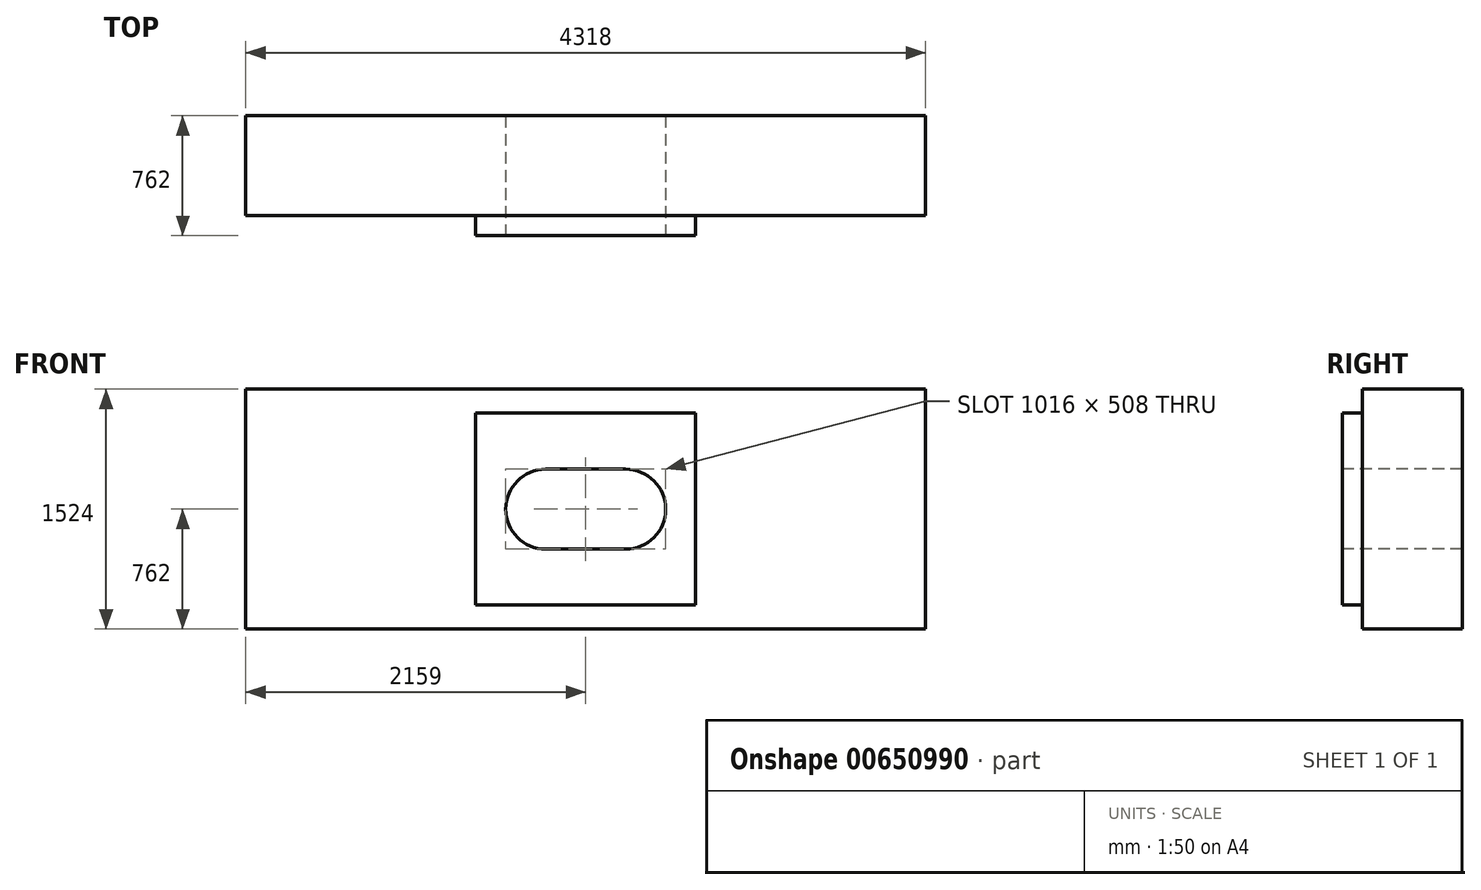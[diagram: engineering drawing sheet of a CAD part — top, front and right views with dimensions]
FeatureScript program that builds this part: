
annotation { "Feature Type Name" : "Feature", "Feature Type Description" : "" }
export const myFeature = defineFeature(function(context is Context, id is Id, definition is map)
    precondition{}
    {
        {
            var Q0;
            Q0=qCreatedBy(makeId("Front.planeOp"),FACE);
            var sketch = newSketch(context, id + "F0", { "sketchPlane" : qUnion([Q0])});
            skLineSegment(sketch, "E0.bottom", {"start": v(2159, -762) * mm, "end": v(-2159, -762) * mm});
            skLineSegment(sketch, "E0.top", {"start": v(2159, 762) * mm, "end": v(-2159, 762) * mm});
            skLineSegment(sketch, "E0.left", {"start": v(2159, -762) * mm, "end": v(2159, 762) * mm});
            skLineSegment(sketch, "E0.right", {"start": v(-2159, -762) * mm, "end": v(-2159, 762) * mm});
            skPoint(sketch, "E0.middle", {"position": v(0, 0) * mm});
            skSolve(sketch);
        }
        {
            var Q0;
            Q0=makeQuery(id+"F0.imprint","IMPRINT",FACE,{"disambiguationData":[TD([[makeQuery(id+"F0.imprint","IMPRINT",EDGE,{"derivedFrom":sQuery(id+"F0.wireOp",EDGE,"E0.bottom")}),-1.0]])]});
            extrude(context, id + "F1", {"entities" : qUnion([Q0]), "depth" : 635 * mm, "offsetDistance" : 25.4 * mm});
        }
        {
            var Q0;
            Q0=makeQuery(id+"F1.opExtrude","CAP_FACE",FACE,{"disambiguationData":[OSD([sQuery(id+"F0.wireOp",EDGE,"E0.bottom"),sQuery(id+"F0.wireOp",EDGE,"E0.top"),sQuery(id+"F0.wireOp",EDGE,"E0.left"),sQuery(id+"F0.wireOp",EDGE,"E0.right")])],"isStart":false});
            var sketch = newSketch(context, id + "F2", { "sketchPlane" : qUnion([Q0])});
            skLineSegment(sketch, "E1.bottom", {"start": v(698.5, -609.6) * mm, "end": v(-698.5, -609.6) * mm});
            skLineSegment(sketch, "E1.top", {"start": v(698.5, 609.6) * mm, "end": v(-698.5, 609.6) * mm});
            skLineSegment(sketch, "E1.left", {"start": v(698.5, -609.6) * mm, "end": v(698.5, 609.6) * mm});
            skLineSegment(sketch, "E1.right", {"start": v(-698.5, -609.6) * mm, "end": v(-698.5, 609.6) * mm});
            skPoint(sketch, "E1.middle", {"position": v(0, 0) * mm});
            skSolve(sketch);
        }
        {
            var Q0;
            Q0=makeQuery(id+"F2.imprint","IMPRINT",FACE,{"disambiguationData":[TD([[makeQuery(id+"F2.imprint","IMPRINT",EDGE,{"derivedFrom":sQuery(id+"F2.wireOp",EDGE,"E1.bottom")}),-1.0]])]});
            extrude(context, id + "F3", {"entities" : qUnion([Q0]), "operationType" : NewBodyOperationType.ADD, "depth" : 127 * mm, "offsetDistance" : 25.4 * mm});
        }
        {
            var Q0;
            Q0=makeQuery(id+"F3.opExtrude","CAP_FACE",FACE,{"disambiguationData":[OSD([sQuery(id+"F2.wireOp",EDGE,"E1.bottom"),sQuery(id+"F2.wireOp",EDGE,"E1.top"),sQuery(id+"F2.wireOp",EDGE,"E1.left"),sQuery(id+"F2.wireOp",EDGE,"E1.right")])],"isStart":false});
            var sketch = newSketch(context, id + "F4", { "sketchPlane" : qUnion([Q0])});
            skLineSegment(sketch, "E2.bottom", {"start": v(254, -254) * mm, "end": v(-254, -254) * mm});
            skLineSegment(sketch, "E2.top", {"start": v(254, 254) * mm, "end": v(-254, 254) * mm});
            skLineSegment(sketch, "E2.left", {"start": v(508, 0) * mm, "end": v(508, 0) * mm});
            skLineSegment(sketch, "E2.right", {"start": v(-508, 0) * mm, "end": v(-508, 0) * mm});
            skPoint(sketch, "E2.middle", {"position": v(0, 0) * mm});
            skPoint(sketch, "E3.visualSharp", {"position": v(-508, 254) * mm});
            skArc(sketch, "E3.filletArc", {"start": v(-501.65, 254) * mm, "mid": v(-506.14, 252.14) * mm, "end": v(-508, 247.65) * mm});
            skPoint(sketch, "E4.visualSharp", {"position": v(508, 254) * mm});
            skArc(sketch, "E4.filletArc", {"start": v(508, 0) * mm, "mid": v(433.6, 179.6) * mm, "end": v(254, 254) * mm});
            skPoint(sketch, "E5.visualSharp", {"position": v(508, -254) * mm});
            skArc(sketch, "E5.filletArc", {"start": v(254, -254) * mm, "mid": v(433.6, -179.6) * mm, "end": v(508, 0) * mm});
            skPoint(sketch, "E6.visualSharp", {"position": v(-508, -254) * mm});
            skArc(sketch, "E6.filletArc", {"start": v(-508, 0) * mm, "mid": v(-433.6, -179.6) * mm, "end": v(-254, -254) * mm});
            skArc(sketch, "E7.filletArc", {"start": v(-254, 254) * mm, "mid": v(-433.6, 179.6) * mm, "end": v(-508, 0) * mm});
            skSolve(sketch);
        }
        {
            var Q0;
            Q0=makeQuery(id+"F4.imprint","IMPRINT",FACE,{"disambiguationData":[TD([[makeQuery(id+"F4.imprint","IMPRINT",EDGE,{"derivedFrom":sQuery(id+"F4.wireOp",EDGE,"E2.bottom")}),-1.0]])]});
            extrude(context, id + "F5", {"entities" : qUnion([Q0]), "operationType" : NewBodyOperationType.REMOVE, "endBound" : BoundingType.THROUGH_ALL, "oppositeDirection" : true, "depth" : 25.4 * mm, "offsetDistance" : 25.4 * mm});
        }
    });
